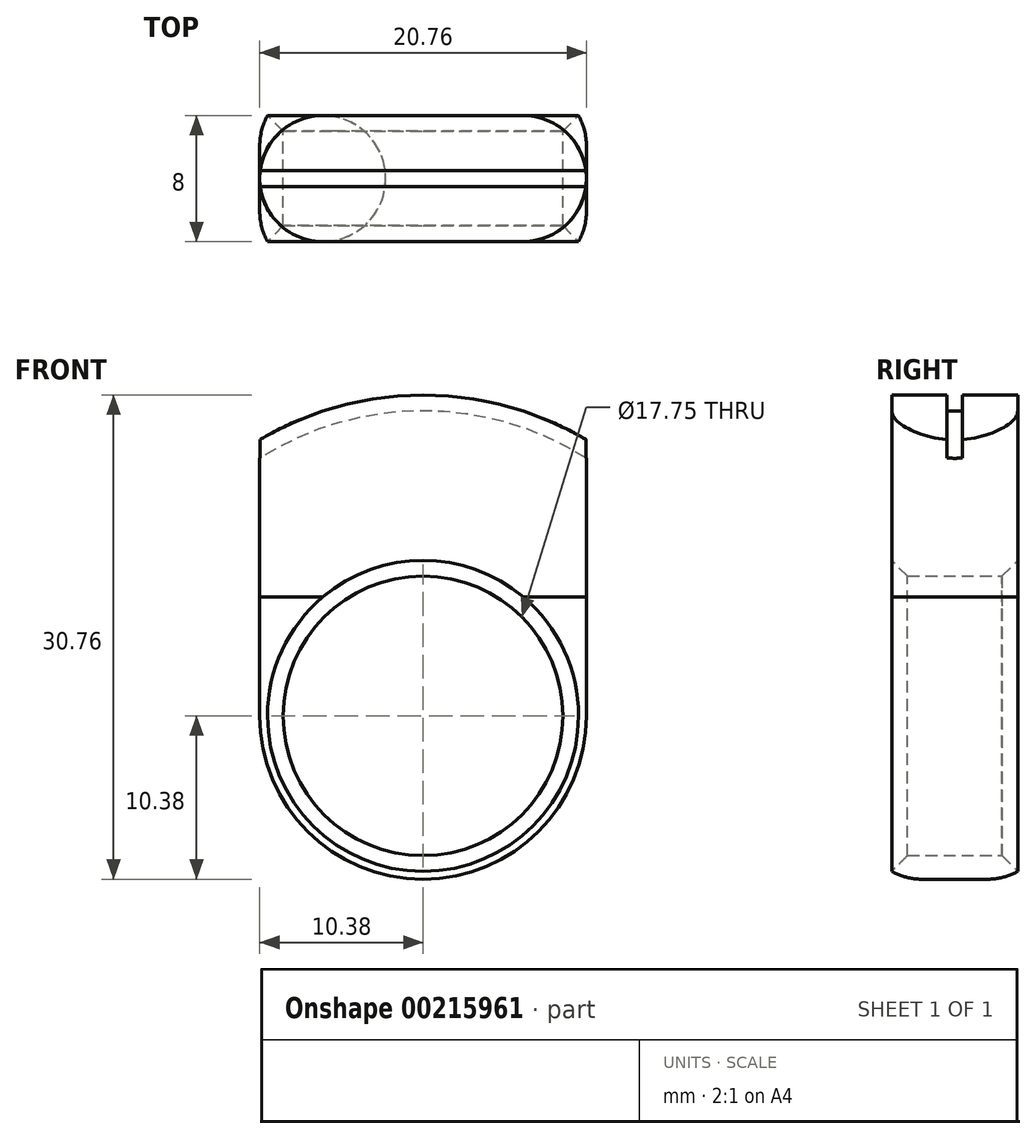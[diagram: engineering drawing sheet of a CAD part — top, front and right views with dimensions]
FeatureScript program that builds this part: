
annotation { "Feature Type Name" : "Feature", "Feature Type Description" : "" }
export const myFeature = defineFeature(function(context is Context, id is Id, definition is map)
    precondition{}
    {
        {
            var Q0;
            Q0=qCreatedBy(makeId("Front.planeOp"),FACE);
            var sketch = newSketch(context, id + "F0", { "sketchPlane" : qUnion([Q0])});
            skCircle(sketch, "E0", {"center": v(0, 0) * mm, "radius": 8.88 * mm});
            skCircle(sketch, "E1.0", {"center": v(0, 0) * mm, "radius": 10.38 * mm});
            skCircle(sketch, "E2.0", {"center": v(0, 0) * mm, "radius": 20.38 * mm});
            skLineSegment(sketch, "E3", {"start": v(10.38, 0) * mm, "end": v(10.38, 17.54) * mm});
            skLineSegment(sketch, "E4.MirrorCS", {"start": v(-10.38, 0) * mm, "end": v(-10.38, 17.54) * mm});
            skCircle(sketch, "E5.0", {"center": v(0, 0) * mm, "radius": 19.38 * mm});
            skSolve(sketch);
        }
        {
            var Q0;
            Q0=makeQuery(id+"F0.imprint","IMPRINT",FACE,{"disambiguationData":[TD([[makeQuery(id+"F0.imprint","IMPRINT",EDGE,{"derivedFrom":sQuery(id+"F0.wireOp",EDGE,"E0")}),-1.0]])]});
            extrude(context, id + "F1", {"entities" : qUnion([Q0]), "depth" : 4 * mm, "hasSecondDirection" : true, "secondDirectionOppositeDirection" : true, "secondDirectionDepth" : 4 * mm});
        }
        {
            var Q0;
            Q0=makeQuery(id+"F1.opExtrude","CAP_EDGE",EDGE,{"disambiguationData":[OSD([sQuery(id+"F0.wireOp",EDGE,"E0")])],"isStart":false});
            var Q1;
            Q1=makeQuery(id+"F1.opExtrude","CAP_EDGE",EDGE,{"disambiguationData":[OSD([sQuery(id+"F0.wireOp",EDGE,"E0")])],"isStart":true});
            chamfer(context, id + "F2", {"entities" : qUnion([Q0, Q1]), "width" : 1 * mm, "tangentPropagation" : true});
        }
        {
            var Q0;
            {var subQ0=sQuery(id+"F0.wireOp",EDGE,"E3");var subQ1=sQuery(id+"F0.wireOp",EDGE,"E1.0");var subQ2=makeQuery(id+"F0.imprint","INTERSECT",VERTEX,{"derivedFrom":[subQ1,subQ0]});Q0=makeQuery(id+"F0.imprint","IMPRINT",FACE,{"disambiguationData":[TD([[makeQuery(id+"F0.imprint","IMPRINT",EDGE,{"disambiguationData":[TD([[subQ2,-1.0]])],"derivedFrom":subQ1}),-1.0]])]});}
            var Q1;
            {var subQ0=sQuery(id+"F0.wireOp",EDGE,"E3");var subQ1=sQuery(id+"F0.wireOp",EDGE,"E2.0");var subQ2=makeQuery(id+"F0.imprint","INTERSECT",VERTEX,{"derivedFrom":[subQ1,subQ0]});Q1=makeQuery(id+"F0.imprint","IMPRINT",FACE,{"disambiguationData":[TD([[makeQuery(id+"F0.imprint","IMPRINT",EDGE,{"disambiguationData":[TD([[subQ2,-1.0]])],"derivedFrom":subQ1}),1.0]])]});}
            extrude(context, id + "F3", {"entities" : qUnion([Q0, Q1]), "operationType" : NewBodyOperationType.ADD, "depth" : 4 * mm, "hasSecondDirection" : true, "secondDirectionOppositeDirection" : true, "secondDirectionDepth" : 4 * mm});
        }
        {
            var Q0;
            {var subQ0=sQuery(id+"F0.wireOp",EDGE,"E3");var subQ1=sQuery(id+"F0.wireOp",EDGE,"E2.0");var subQ2=makeQuery(id+"F0.imprint","INTERSECT",VERTEX,{"derivedFrom":[subQ1,subQ0]});Q0=makeQuery(id+"F0.imprint","IMPRINT",FACE,{"disambiguationData":[TD([[makeQuery(id+"F0.imprint","IMPRINT",EDGE,{"disambiguationData":[TD([[subQ2,-1.0]])],"derivedFrom":subQ1}),1.0]])]});}
            extrude(context, id + "F4", {"entities" : qUnion([Q0]), "operationType" : NewBodyOperationType.REMOVE, "oppositeDirection" : true, "depth" : .5 * mm, "hasSecondDirection" : true, "secondDirectionOppositeDirection" : false, "secondDirectionDepth" : .5 * mm});
        }
        {
            var Q0;
            Q0=makeQuery(id+"F3.opExtrude","CAP_EDGE",EDGE,{"disambiguationData":[OSD([sQuery(id+"F0.wireOp",EDGE,"E3")])],"isStart":false});
            var Q1;
            Q1=makeQuery(id+"F3.opExtrude","CAP_EDGE",EDGE,{"disambiguationData":[OSD([sQuery(id+"F0.wireOp",EDGE,"E3")])],"isStart":true});
            var Q2;
            Q2=makeQuery(id+"F3.opExtrude","CAP_EDGE",EDGE,{"disambiguationData":[OSD([sQuery(id+"F0.wireOp",EDGE,"E4.MirrorCS")])],"isStart":false});
            var Q3;
            Q3=makeQuery(id+"F3.opExtrude","CAP_EDGE",EDGE,{"disambiguationData":[OSD([sQuery(id+"F0.wireOp",EDGE,"E4.MirrorCS")])],"isStart":true});
            fillet(context, id + "F5", {"entities" : qUnion([Q0, Q1, Q2, Q3]), "radius" : 4 * mm, "tangentPropagation" : true, "allowEdgeOverflow" : false});
        }
    });
